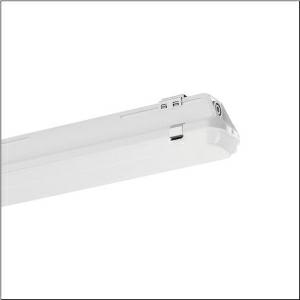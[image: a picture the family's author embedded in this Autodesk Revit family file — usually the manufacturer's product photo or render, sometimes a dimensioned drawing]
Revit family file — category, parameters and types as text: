
# Revit family: monsun_r__21_51fb10mp380c_daa5
name_source: partatom
category: Lighting Fixtures
units: mm (PartAtom-declared; Revit-internal decimal feet)

## family parameters
Cut with Voids When Loaded = No
Host = Face
Light Source = No
Part Type = Normal
Room Calculation Point = No
Round Connector Dimension = Use Diameter
Shared = No

## types (1)
- --- (1 x LED, 8490 lm, 49.1 W, 3000K)
    Apparent Load = 49 VA
    CIE Flux Codes = 47 77 93 94 100
    Color Rendering = 80
    Color Temperature = 3000K
    Default Elevation = 1800 mm
    Description = Monsun® 21, damp-proof luminaire, chain hanger, primary optical cover: enclosure, of PMMA, light emission: direct distribution, primary light characteristic: symmetric, installation type: suspended mounting, surface-mounted, horizontal mounting, vertical mounting, LED, rated luminous flux: 8.490lm, luminous efficacy: 173lm/W, light colour: 830, colour temperature: 3000K, control gear: ON/OFF Multilumen, with terminal, 3-pole, max. 2.5mm², mains connection: 220..240V, AC, 50/60Hz, rated input power: 49W, housing, of glass-fibre reinforced polyester, uncoated, bright grey, incl. chain hanger, length: 1.590mm, width: 90mm, height: 88mm, clip for enclosure, of stainless steel (V2A), ceiling mounting element, of stainless steel (V2A), chain hanger, of stainless steel (V2A), protection rating (complete): IP66, insulation class (complete): insulation class I (protective earthing), certification: CE, ENEC, VDE, UKCA, protection symbol: D, impact resistance: IK04, permissible operating ambient temperature: -25..+35°C, standard: EN 50419, EN 60598-2-1, corresponds to IFS (International Featured Standards) requirements for safety and quality in the food industry, for indoor or canopied outdoor use, no direct snow, no direct sun, no direct rain, LABS conformity tested according to VDMA 24364:2018-05, contact your sales advisor before using the luminaires in applications with unclear chemical exposure, large temperature fluctuations or condensation-forming humidity, packaging unit: 1 piece
    Height = 89 mm
    Lamp = 1 x LED
    Lamp Light Flux = 8490 lm
    Lamp Power = 49.1 W
    Lamp count = 1
    Length = 1590 mm
    Luminous efficacy = 173 lm/W
    Manufacturer = Siteco
    ModVariant = No
    Model = 51FB10MP380C
    Mounting Place = Ceiling
    Mounting Type = Surface mounted
    Number of Poles = 1
    OnlyDefault = Yes
    Power Factor = 1
    Product Name = Monsun® 21
    Product group = damp-proof luminaire
    ProductGroupID = 300
    Protection Class = Protection class I
    Protection Degree = IP 66
    RLX_Detail_Level = 1
    RLX_Emergency_Light_Flux = 0 lm
    RLX_Emergency_Type = 0
    RLX_Emergency_Type_DB = No
    RlxData = <blob elided: 89809 chars, md5=295e6af2>
    Socket = socket
    Standby Power = 0 W
    System Light Flux = 8490 lm
    System Power = 49 W
    Type Comments = factory setting: luminous flux: 100 % | (A | C | E) | 114 mA
    Type Image = l_1319656.jpg
    URL = http://relux.com
    VarID = @adj_031810
    Voltage = 0 V
    Weight = 0.00 kg
    Width = 90 mm

## geometry (parser evidence)
native form markers: Blend x4, Sweep x14
no freeform markers — native parametric forms only
